# Revit family: RN 26035 Rubinetto a sfera a 3 componenti
name_source: partatom
category: Rohrzubehör
units: mm (PartAtom-declared; Revit-internal decimal feet)

## family parameters
Arbeitsebenenbasiert = Nein
Beim Laden mit Abzugskörper schneiden = Nein
Bemaßung runder Anschluss = Durchmesser verwenden
Gemeinsam genutzt = Nein
Immer vertikal = Ja
Teiletyp = Ventil - Zerlegung in

## types (9) — shared parameters
1.010.00.2 Number of the part of the guideline = 2
1.010.00.3 Issue date (month) of the guideline = 201601
1.010.00.4 Manufacturer name = R. Nussbaum AG
1.010.00.5 Revision date of the file = 20190514
1.100.00.3 Sort number for display sequence = 4
1.100.00.4 Product designation = Absperr- und Regelarmaturen
1.960/3L.00.8 Link (URL) = https://www.nussbaum.ch
2.700.00.4 valve assembly type = 11
2.700.00.7 maximum operating temperature TB [°C] = 100
2.700.00.8 maximum operating pressure(working pressure) ps [1.0 · 102 Pa] = 16
Connector Visibility = Nein
EnclosingSpace Visibility = Nein
Hersteller = R. Nussbauzm AG
Modell = 0
URL = https://www.nussbaum.ch

## per-type parameters (varying)
- DN 15: 1.800.00.3 BS number=0040170000000000000000000000090070000000000000000300000000; 1.810.00.3 Manufacturer’s reference number=26035.54; 1.810.00.4 DATANORM number=26035.54; 1.810.00.6 GTIN number=7612945704320; 2.700.00.26 product description=26035.54, Kugelhahn 3-teilig, Edelstahl, DN=15, Rp=½; 2.700.00.5 nominal size DN=15; 2.700.00.6 kvs-value [m3/h]=35; CONNECTOR0_DIAMETER_dX_0r=15 mm; CONNECTOR0_dX_00=30 mm; CONNECTOR0_dX_01=17 mm; CONNECTOR0_ref_dX=17 mm; CONNECTOR1_DIAMETER_dX_0r=15 mm; CONNECTOR1_dX_00=17 mm; CONNECTOR1_dX_01=30 mm; CONNECTOR1_ref_dX=17 mm; R. Nussbaum AG 26035.54 en Visibility=Ja; R. Nussbaum AG 26035.55 en Visibility=Nein; R. Nussbaum AG 26035.56 en Visibility=Nein; R. Nussbaum AG 26035.57 en Visibility=Nein; R. Nussbaum AG 26035.58 en Visibility=Nein; R. Nussbaum AG 26035.59 en Visibility=Nein; R. Nussbaum AG 26035.60 en Visibility=Nein; R. Nussbaum AG 26035.61 en Visibility=Nein; R. Nussbaum AG 26035.62 en Visibility=Nein; Typenkommentare=Valvola d'arrestoDN 15
- DN 20: 1.800.00.3 BS number=0040170000000000000000000000090070000000000000000400000000; 1.810.00.3 Manufacturer’s reference number=26035.55; 1.810.00.4 DATANORM number=26035.55; 1.810.00.6 GTIN number=7612945704337; 2.700.00.26 product description=26035.55, Kugelhahn 3-teilig, Edelstahl, DN=20, Rp=¾; 2.700.00.5 nominal size DN=20; 2.700.00.6 kvs-value [m3/h]=47; CONNECTOR0_DIAMETER_dX_0r=20 mm; CONNECTOR0_dX_00=35 mm; CONNECTOR0_dX_01=20 mm; CONNECTOR0_ref_dX=20 mm; CONNECTOR1_DIAMETER_dX_0r=20 mm; CONNECTOR1_dX_00=20 mm; CONNECTOR1_dX_01=35 mm; CONNECTOR1_ref_dX=20 mm; R. Nussbaum AG 26035.54 en Visibility=Nein; R. Nussbaum AG 26035.55 en Visibility=Ja; R. Nussbaum AG 26035.56 en Visibility=Nein; R. Nussbaum AG 26035.57 en Visibility=Nein; R. Nussbaum AG 26035.58 en Visibility=Nein; R. Nussbaum AG 26035.59 en Visibility=Nein; R. Nussbaum AG 26035.60 en Visibility=Nein; R. Nussbaum AG 26035.61 en Visibility=Nein; R. Nussbaum AG 26035.62 en Visibility=Nein; Typenkommentare=Valvola d'arrestoDN 20
- DN 25: 1.800.00.3 BS number=0040170000000000000000000000090070000000000000000500000000; 1.810.00.3 Manufacturer’s reference number=26035.56; 1.810.00.4 DATANORM number=26035.56; 1.810.00.6 GTIN number=7612945704344; 2.700.00.26 product description=26035.56, Kugelhahn 3-teilig, Edelstahl, DN=25, Rp=1; 2.700.00.5 nominal size DN=25; 2.700.00.6 kvs-value [m3/h]=54; CONNECTOR0_DIAMETER_dX_0r=25 mm  [stored 0.082021 ft]; CONNECTOR0_dX_00=40 mm; CONNECTOR0_dX_01=24 mm; CONNECTOR0_ref_dX=24 mm; CONNECTOR1_DIAMETER_dX_0r=25 mm  [stored 0.082021 ft]; CONNECTOR1_dX_00=24 mm; CONNECTOR1_dX_01=40 mm; CONNECTOR1_ref_dX=24 mm; R. Nussbaum AG 26035.54 en Visibility=Nein; R. Nussbaum AG 26035.55 en Visibility=Nein; R. Nussbaum AG 26035.56 en Visibility=Ja; R. Nussbaum AG 26035.57 en Visibility=Nein; R. Nussbaum AG 26035.58 en Visibility=Nein; R. Nussbaum AG 26035.59 en Visibility=Nein; R. Nussbaum AG 26035.60 en Visibility=Nein; R. Nussbaum AG 26035.61 en Visibility=Nein; R. Nussbaum AG 26035.62 en Visibility=Nein; Typenkommentare=Valvola d'arrestoDN 25
- DN 32: 1.800.00.3 BS number=0040170000000000000000000000090070000000000000000600000000; 1.810.00.3 Manufacturer’s reference number=26035.57; 1.810.00.4 DATANORM number=26035.57; 1.810.00.6 GTIN number=7612945704351; 2.700.00.26 product description=26035.57, Kugelhahn 3-teilig, Edelstahl, DN=32, Rp=1¼; 2.700.00.5 nominal size DN=32; 2.700.00.6 kvs-value [m3/h]=82; CONNECTOR0_DIAMETER_dX_0r=32 mm; CONNECTOR0_dX_00=49 mm; CONNECTOR0_dX_01=30 mm; CONNECTOR0_ref_dX=30 mm; CONNECTOR1_DIAMETER_dX_0r=32 mm; CONNECTOR1_dX_00=30 mm; CONNECTOR1_dX_01=49 mm; CONNECTOR1_ref_dX=30 mm; R. Nussbaum AG 26035.54 en Visibility=Nein; R. Nussbaum AG 26035.55 en Visibility=Nein; R. Nussbaum AG 26035.56 en Visibility=Nein; R. Nussbaum AG 26035.57 en Visibility=Ja; R. Nussbaum AG 26035.58 en Visibility=Nein; R. Nussbaum AG 26035.59 en Visibility=Nein; R. Nussbaum AG 26035.60 en Visibility=Nein; R. Nussbaum AG 26035.61 en Visibility=Nein; R. Nussbaum AG 26035.62 en Visibility=Nein; Typenkommentare=Valvola d'arrestoDN 32
- DN 40: 1.800.00.3 BS number=0040170000000000000000000000090070000000000000000700000000; 1.810.00.3 Manufacturer’s reference number=26035.58; 1.810.00.4 DATANORM number=26035.58; 1.810.00.6 GTIN number=7612945704368; 2.700.00.26 product description=26035.58, Kugelhahn 3-teilig, Edelstahl, DN=40, Rp=1½; 2.700.00.5 nominal size DN=40; 2.700.00.6 kvs-value [m3/h]=160; CONNECTOR0_DIAMETER_dX_0r=40 mm; CONNECTOR0_dX_00=55 mm; CONNECTOR0_dX_01=38 mm; CONNECTOR0_ref_dX=38 mm; CONNECTOR1_DIAMETER_dX_0r=40 mm; CONNECTOR1_dX_00=38 mm; CONNECTOR1_dX_01=55 mm; CONNECTOR1_ref_dX=38 mm; R. Nussbaum AG 26035.54 en Visibility=Nein; R. Nussbaum AG 26035.55 en Visibility=Nein; R. Nussbaum AG 26035.56 en Visibility=Nein; R. Nussbaum AG 26035.57 en Visibility=Nein; R. Nussbaum AG 26035.58 en Visibility=Ja; R. Nussbaum AG 26035.59 en Visibility=Nein; R. Nussbaum AG 26035.60 en Visibility=Nein; R. Nussbaum AG 26035.61 en Visibility=Nein; R. Nussbaum AG 26035.62 en Visibility=Nein; Typenkommentare=Valvola d'arrestoDN 40
- DN 50: 1.800.00.3 BS number=0040170000000000000000000000090070000000000000000800000000; 1.810.00.3 Manufacturer’s reference number=26035.59; 1.810.00.4 DATANORM number=26035.59; 1.810.00.6 GTIN number=7612945704375; 2.700.00.26 product description=26035.59, Kugelhahn 3-teilig, Edelstahl, DN=50, Rp=2; 2.700.00.5 nominal size DN=50; 2.700.00.6 kvs-value [m3/h]=230; CONNECTOR0_DIAMETER_dX_0r=50 mm; CONNECTOR0_dX_00=64 mm; CONNECTOR0_dX_01=48 mm  [stored 0.15748 ft]; CONNECTOR0_ref_dX=48 mm  [stored 0.15748 ft]; CONNECTOR1_DIAMETER_dX_0r=50 mm; CONNECTOR1_dX_00=48 mm  [stored 0.15748 ft]; CONNECTOR1_dX_01=64 mm; CONNECTOR1_ref_dX=48 mm  [stored 0.15748 ft]; R. Nussbaum AG 26035.54 en Visibility=Nein; R. Nussbaum AG 26035.55 en Visibility=Nein; R. Nussbaum AG 26035.56 en Visibility=Nein; R. Nussbaum AG 26035.57 en Visibility=Nein; R. Nussbaum AG 26035.58 en Visibility=Nein; R. Nussbaum AG 26035.59 en Visibility=Ja; R. Nussbaum AG 26035.60 en Visibility=Nein; R. Nussbaum AG 26035.61 en Visibility=Nein; R. Nussbaum AG 26035.62 en Visibility=Nein; Typenkommentare=Valvola d'arrestoDN 50
- DN 65: 1.800.00.3 BS number=0040170000000000000000000000090070000000000000000900000000; 1.810.00.3 Manufacturer’s reference number=26035.60; 1.810.00.4 DATANORM number=26035.60; 1.810.00.6 GTIN number=7612945704382; 2.700.00.26 product description=26035.60, Kugelhahn 3-teilig, Edelstahl, DN=65, Rp=2½; 2.700.00.5 nominal size DN=65; 2.700.00.6 kvs-value [m3/h]=510; CONNECTOR0_DIAMETER_dX_0r=65 mm; CONNECTOR0_dX_00=80 mm; CONNECTOR0_dX_01=53 mm; CONNECTOR0_ref_dX=53 mm; CONNECTOR1_DIAMETER_dX_0r=65 mm; CONNECTOR1_dX_00=53 mm; CONNECTOR1_dX_01=80 mm; CONNECTOR1_ref_dX=53 mm; R. Nussbaum AG 26035.54 en Visibility=Nein; R. Nussbaum AG 26035.55 en Visibility=Nein; R. Nussbaum AG 26035.56 en Visibility=Nein; R. Nussbaum AG 26035.57 en Visibility=Nein; R. Nussbaum AG 26035.58 en Visibility=Nein; R. Nussbaum AG 26035.59 en Visibility=Nein; R. Nussbaum AG 26035.60 en Visibility=Ja; R. Nussbaum AG 26035.61 en Visibility=Nein; R. Nussbaum AG 26035.62 en Visibility=Nein; Typenkommentare=Valvola d'arrestoDN 65
- DN 80: 1.800.00.3 BS number=0040170000000000000000000000090070000000000000001000000000; 1.810.00.3 Manufacturer’s reference number=26035.61; 1.810.00.4 DATANORM number=26035.61; 1.810.00.6 GTIN number=7612945704399; 2.700.00.26 product description=26035.61, Kugelhahn 3-teilig, Edelstahl, DN=80, Rp=3; 2.700.00.5 nominal size DN=80; 2.700.00.6 kvs-value [m3/h]=797; CONNECTOR0_DIAMETER_dX_0r=80 mm; CONNECTOR0_dX_00=88 mm; CONNECTOR0_dX_01=61 mm; CONNECTOR0_ref_dX=61 mm; CONNECTOR1_DIAMETER_dX_0r=80 mm; CONNECTOR1_dX_00=61 mm; CONNECTOR1_dX_01=88 mm; CONNECTOR1_ref_dX=61 mm; R. Nussbaum AG 26035.54 en Visibility=Nein; R. Nussbaum AG 26035.55 en Visibility=Nein; R. Nussbaum AG 26035.56 en Visibility=Nein; R. Nussbaum AG 26035.57 en Visibility=Nein; R. Nussbaum AG 26035.58 en Visibility=Nein; R. Nussbaum AG 26035.59 en Visibility=Nein; R. Nussbaum AG 26035.60 en Visibility=Nein; R. Nussbaum AG 26035.61 en Visibility=Ja; R. Nussbaum AG 26035.62 en Visibility=Nein; Typenkommentare=Valvola d'arrestoDN 80
- DN 100: 1.800.00.3 BS number=0040170000000000000000000000090070000000000000001100000000; 1.810.00.3 Manufacturer’s reference number=26035.62; 1.810.00.4 DATANORM number=26035.62; 1.810.00.6 GTIN number=7612945704412; 2.700.00.26 product description=26035.62, Kugelhahn 3-teilig, Edelstahl, DN=100, Rp=4; 2.700.00.5 nominal size DN=100; 2.700.00.6 kvs-value [m3/h]=1297; CONNECTOR0_DIAMETER_dX_0r=100 mm  [stored 0.328084 ft]; CONNECTOR0_dX_00=110 mm  [stored 0.360892 ft]; CONNECTOR0_dX_01=97 mm; CONNECTOR0_ref_dX=97 mm; CONNECTOR1_DIAMETER_dX_0r=100 mm  [stored 0.328084 ft]; CONNECTOR1_dX_00=97 mm; CONNECTOR1_dX_01=110 mm  [stored 0.360892 ft]; CONNECTOR1_ref_dX=97 mm; R. Nussbaum AG 26035.54 en Visibility=Nein; R. Nussbaum AG 26035.55 en Visibility=Nein; R. Nussbaum AG 26035.56 en Visibility=Nein; R. Nussbaum AG 26035.57 en Visibility=Nein; R. Nussbaum AG 26035.58 en Visibility=Nein; R. Nussbaum AG 26035.59 en Visibility=Nein; R. Nussbaum AG 26035.60 en Visibility=Nein; R. Nussbaum AG 26035.61 en Visibility=Nein; R. Nussbaum AG 26035.62 en Visibility=Ja; Typenkommentare=Valvola d'arrestoDN 100

note: [stored X ft] marks values corroborated as IEEE doubles in the binary element streams (Revit-internal decimal feet)

## geometry (parser evidence)
native form markers: Sweep x3
no freeform markers — native parametric forms only
